# Revit family: Hager-VECTOR-Surface_mounted-IP65-With_Cover-With_DIN-NoHosted-GB-en
name_source: partatom
category: Electrical Equipment
units: mm (PartAtom-declared; Revit-internal decimal feet)

## family parameters
Always vertical = Yes
Cut with Voids When Loaded = No
Maintain Annotation Orientation = No
Panel Configuration = Two Columns, Circuits Across
Part Type = Panelboard
Room Calculation Point = No
Round Connector Dimension = Use Diameter
Shared = No
Work Plane-Based = Yes

## types (15) — shared parameters
Code hager = ADD-EC000214_EU
Default Elevation = 1200 mm
EF000003 - Mounting method = Surface mounted
EF000024 - UV resistant = No
EF000116 - RAL-number = 7035
EF000118 - With mounting plate = No
EF001062 - EMC-version = No
EF001134 - DIN-rail = Yes
EF005474 - Degree of protection (IP) = IP65
EF006306 - With lock = No
ETIM class code = EC000214
ETIM class name = Small distribution board
HG000001-Number of columns = 1
HG000002-With door or cover = Yes
HG000003-Range = VECTOR
HG000005-Thickness = 2 mm  [stored 0.00656168 ft]
HG000006-Flush mounted = No
HG000009-Double swing door = No
HG000010-Asymmetric doors = No
HG000011-Empty rows from bottom = No
HG000012-Door swing angle = 90.00°
HG000013-Door on the left = No
HG000014-Door on the right = Yes
HG000015-Clearance visibility = Yes
HG000016-Door 3D visibility = Yes
HG000017-Distance between poles = 18 mm  [stored 0.0590551 ft]
HG000060-RAL-number = 7035
HG000099-Onfly Template ID = 507532
Manufacturer = Hager
Name BIM&CO = Electricity
Name hager = ADD_Enclosures_EC000214
Reference = Template-Enclosure_EU-EC000214
Uniformat = Low Tension Service & Dist.
Uniformat code = D501001
zero-valued in all types: EF000218 - Built-in depth, EF000332 - Built-in height, EF000846 - Built-in width, EF001131 - Inner depth, HG000007-Number of empty columns, HG000008-Number of empty rows

## per-type parameters (varying)
| type | BC_METADATA | EF000007 - Colour | EF000008 - Width | EF000040 - Height | EF000049 - Depth | EF000266 - Number of rows | EF001088 - Extension possible | EF002950 - Width in number of modular spacings | EF004462 - Type of closure | EF006244 - Transparent cover/door | EF009212 - Cover model | EF015776 - Earthing terminal block | EF015777 - Neutral terminal block | EF015941 - Signal passing door | HG000004-Manufacturer reference | HGEF000266-Number of rows | HGEF002950-Width in number of modular spacings |
| VECTOR-Surface_mounted_W111_H175_D93_0_Modular_Spacing-VE103L | {"ObjectGuid":"cf184432-3cd7-4e5f-ada6-339d770f1633","ModelGuid":"a7e1683c-11b9-4448-ba98-b7f7af68d92b","VariantGuid":"b056254d-3ef2-4c93-8cda-b86145ad0995","Revision":"#5","VariantName":"VECTOR-Surface_mounted_W111_H175_D93_0_Modular_Spacing-VE103L"} |  | 111 mm | 175 mm  [stored 0.574147 ft] | 93 mm  [stored 0.305118 ft] | 1 | No | 0 |  | No |  | No | No | No | VE103L | 1 | 0 |
| VECTOR-Surface_mounted_W111_H175_D93_3_Modular_Spacing-VE103U | {"ObjectGuid":"cf184432-3cd7-4e5f-ada6-339d770f1633","ModelGuid":"a7e1683c-11b9-4448-ba98-b7f7af68d92b","VariantGuid":"33b98be7-e844-4ef4-b4b9-70a6d8c90a68","Revision":"#5","VariantName":"VECTOR-Surface_mounted_W111_H175_D93_3_Modular_Spacing-VE103U"} | Grey | 111 mm | 175 mm  [stored 0.574147 ft] | 93 mm  [stored 0.305118 ft] | 1 | Yes | 3 | Other | Yes | Closed | No | No | Yes | VE103U | 1 | 3 |
| VECTOR-Surface_mounted_W164_H190_D113_6_Modular_Spacing-VE106D | {"ObjectGuid":"cf184432-3cd7-4e5f-ada6-339d770f1633","ModelGuid":"a7e1683c-11b9-4448-ba98-b7f7af68d92b","VariantGuid":"a9786216-0ab6-4341-b900-c5e8849a9ae5","Revision":"#5","VariantName":"VECTOR-Surface_mounted_W164_H190_D113_6_Modular_Spacing-VE106D"} | Grey | 164 mm  [stored 0.538058 ft] | 190 mm  [stored 0.62336 ft] | 113 mm  [stored 0.370735 ft] | 1 | Yes | 6 | Other | Yes | Closed | Yes | No | Yes | VE106D | 1 | 6 |
| VECTOR-Surface_mounted_W165_H190_D113_6_Modular_Spacing-VE106R | {"ObjectGuid":"cf184432-3cd7-4e5f-ada6-339d770f1633","ModelGuid":"a7e1683c-11b9-4448-ba98-b7f7af68d92b","VariantGuid":"00ca3daa-a91f-4168-81a1-5edfcb0f272f","Revision":"#5","VariantName":"VECTOR-Surface_mounted_W165_H190_D113_6_Modular_Spacing-VE106R"} | Grey | 165 mm | 190 mm  [stored 0.62336 ft] | 113 mm  [stored 0.370735 ft] | 1 | Yes | 6 | Other | Yes | Closed | Yes | No | Yes | VE106R | 1 | 6 |
| VECTOR-Surface_mounted_W165_H190_D113_6_Modular_Spacing-VE106U | {"ObjectGuid":"cf184432-3cd7-4e5f-ada6-339d770f1633","ModelGuid":"a7e1683c-11b9-4448-ba98-b7f7af68d92b","VariantGuid":"ff6ab4a2-17f5-46e5-9e6c-958d5859923b","Revision":"#5","VariantName":"VECTOR-Surface_mounted_W165_H190_D113_6_Modular_Spacing-VE106U"} | Grey | 165 mm | 190 mm  [stored 0.62336 ft] | 113 mm  [stored 0.370735 ft] | 1 | Yes | 6 | Other | Yes | With notch | Yes | Yes | Yes | VE106U | 1 | 6 |
| VECTOR-Surface_mounted_W237_H210_D114_10_Modular_Spacing-VE110L | {"ObjectGuid":"cf184432-3cd7-4e5f-ada6-339d770f1633","ModelGuid":"a7e1683c-11b9-4448-ba98-b7f7af68d92b","VariantGuid":"f6819492-bbc3-4100-a5d4-2ab26a7b28ed","Revision":"#5","VariantName":"VECTOR-Surface_mounted_W237_H210_D114_10_Modular_Spacing-VE110L"} | Grey | 237 mm  [stored 0.777559 ft] | 210 mm  [stored 0.688976 ft] | 114 mm  [stored 0.374016 ft] | 1 | Yes | 10 | Other | Yes | With notch | Yes | Yes | Yes | VE110L | 1 | 10 |
| VECTOR-Surface_mounted_W237_H210_D114_10_Modular_Spacing-VE110U | {"ObjectGuid":"cf184432-3cd7-4e5f-ada6-339d770f1633","ModelGuid":"a7e1683c-11b9-4448-ba98-b7f7af68d92b","VariantGuid":"e1947f42-2fa9-422b-868e-21b958eb2752","Revision":"#5","VariantName":"VECTOR-Surface_mounted_W237_H210_D114_10_Modular_Spacing-VE110U"} | Grey | 237 mm  [stored 0.777559 ft] | 210 mm  [stored 0.688976 ft] | 114 mm  [stored 0.374016 ft] | 1 | Yes | 10 | Other | Yes | With notch | Yes | Yes | Yes | VE110U | 1 | 10 |
| VECTOR-Surface_mounted_W310_H302_D151_12_Modular_Spacing-VE112R | {"ObjectGuid":"cf184432-3cd7-4e5f-ada6-339d770f1633","ModelGuid":"a7e1683c-11b9-4448-ba98-b7f7af68d92b","VariantGuid":"4535648d-e49a-477f-b244-be2d15d3d02b","Revision":"#5","VariantName":"VECTOR-Surface_mounted_W310_H302_D151_12_Modular_Spacing-VE112R"} | Grey | 310 mm  [stored 1.01706 ft] | 302 mm  [stored 0.990814 ft] | 151 mm  [stored 0.495407 ft] | 1 | Yes | 12 | Other | Yes | Closed | Yes | No | Yes | VE112R | 1 | 12 |
| VECTOR-Surface_mounted_W310_H302_D151_12_Modular_Spacing-VE112U | {"ObjectGuid":"cf184432-3cd7-4e5f-ada6-339d770f1633","ModelGuid":"a7e1683c-11b9-4448-ba98-b7f7af68d92b","VariantGuid":"a9ebdbd7-57ce-487c-afcb-f5184dba4357","Revision":"#5","VariantName":"VECTOR-Surface_mounted_W310_H302_D151_12_Modular_Spacing-VE112U"} | Grey | 310 mm  [stored 1.01706 ft] | 302 mm  [stored 0.990814 ft] | 151 mm  [stored 0.495407 ft] | 1 | Yes | 12 | Other | Yes | With notch | Yes | Yes | Yes | VE112U | 1 | 12 |
| VECTOR-Surface_mounted_W418_H302_D151_18_Modular_Spacing-VE118R | {"ObjectGuid":"cf184432-3cd7-4e5f-ada6-339d770f1633","ModelGuid":"a7e1683c-11b9-4448-ba98-b7f7af68d92b","VariantGuid":"952289d8-8b83-40db-8a5c-b9a80e3fe287","Revision":"#5","VariantName":"VECTOR-Surface_mounted_W418_H302_D151_18_Modular_Spacing-VE118R"} | Grey | 418 mm  [stored 1.37139 ft] | 302 mm  [stored 0.990814 ft] | 151 mm  [stored 0.495407 ft] | 1 | Yes | 18 | Other | No | Closed | No | No | Yes | VE118R | 1 | 18 |
| VECTOR-Surface_mounted_W310_H427_D151_12_Modular_Spacing-VE212R | {"ObjectGuid":"cf184432-3cd7-4e5f-ada6-339d770f1633","ModelGuid":"a7e1683c-11b9-4448-ba98-b7f7af68d92b","VariantGuid":"b669b9a5-dde1-4271-a41a-f58e277a09bf","Revision":"#5","VariantName":"VECTOR-Surface_mounted_W310_H427_D151_12_Modular_Spacing-VE212R"} | Grey | 310 mm  [stored 1.01706 ft] | 427 mm  [stored 1.40092 ft] | 151 mm  [stored 0.495407 ft] | 2 | Yes | 12 | Other | Yes | Closed | Yes | No | Yes | VE212R | 2 | 12 |
| VECTOR-Surface_mounted_W310_H427_D151_12_Modular_Spacing-VE212U | {"ObjectGuid":"cf184432-3cd7-4e5f-ada6-339d770f1633","ModelGuid":"a7e1683c-11b9-4448-ba98-b7f7af68d92b","VariantGuid":"bbd8290d-e69e-48c8-9a8c-90d4f08b2e47","Revision":"#5","VariantName":"VECTOR-Surface_mounted_W310_H427_D151_12_Modular_Spacing-VE212U"} | Grey | 310 mm  [stored 1.01706 ft] | 427 mm  [stored 1.40092 ft] | 151 mm  [stored 0.495407 ft] | 2 | Yes | 12 | Other | Yes | With notch | Yes | Yes | Yes | VE212U | 2 | 12 |
| VECTOR-Surface_mounted_W418_H452_D151_18_Modular_Spacing-VE218R | {"ObjectGuid":"cf184432-3cd7-4e5f-ada6-339d770f1633","ModelGuid":"a7e1683c-11b9-4448-ba98-b7f7af68d92b","VariantGuid":"f1e5f5bc-e5c7-4e73-8110-19c560439327","Revision":"#5","VariantName":"VECTOR-Surface_mounted_W418_H452_D151_18_Modular_Spacing-VE218R"} | Grey | 418 mm  [stored 1.37139 ft] | 452 mm  [stored 1.48294 ft] | 151 mm  [stored 0.495407 ft] | 2 | Yes | 18 | Other | Yes | Closed | No | No | Yes | VE218R | 2 | 18 |
| VECTOR-Surface_mounted_W310_H552_D151_12_Modular_Spacing-VE312R | {"ObjectGuid":"cf184432-3cd7-4e5f-ada6-339d770f1633","ModelGuid":"a7e1683c-11b9-4448-ba98-b7f7af68d92b","VariantGuid":"c78415cd-e98c-43b6-a46f-78d0d30cd1dc","Revision":"#5","VariantName":"VECTOR-Surface_mounted_W310_H552_D151_12_Modular_Spacing-VE312R"} | Grey | 310 mm  [stored 1.01706 ft] | 552 mm  [stored 1.81102 ft] | 151 mm  [stored 0.495407 ft] | 3 | Yes | 12 | Other | Yes | Closed | No | No | Yes | VE312R | 3 | 12 |
| VECTOR-Surface_mounted_W418_H602_D151_18_Modular_Spacing-VE318Y | {"ObjectGuid":"cf184432-3cd7-4e5f-ada6-339d770f1633","ModelGuid":"a7e1683c-11b9-4448-ba98-b7f7af68d92b","VariantGuid":"6c1ea4a3-3c42-4c44-a16f-1f63f870ad36","Revision":"#5","VariantName":"VECTOR-Surface_mounted_W418_H602_D151_18_Modular_Spacing-VE318Y"} | Grey | 418 mm  [stored 1.37139 ft] | 602 mm  [stored 1.97507 ft] | 151 mm  [stored 0.495407 ft] | 3 | Yes | 18 | Other | Yes | Closed | No | No | Yes | VE318Y | 3 | 18 |

note: [stored X ft] marks values corroborated as IEEE doubles in the binary element streams (Revit-internal decimal feet)

## geometry (parser evidence)
native form markers: Sweep x15
no freeform markers — native parametric forms only
